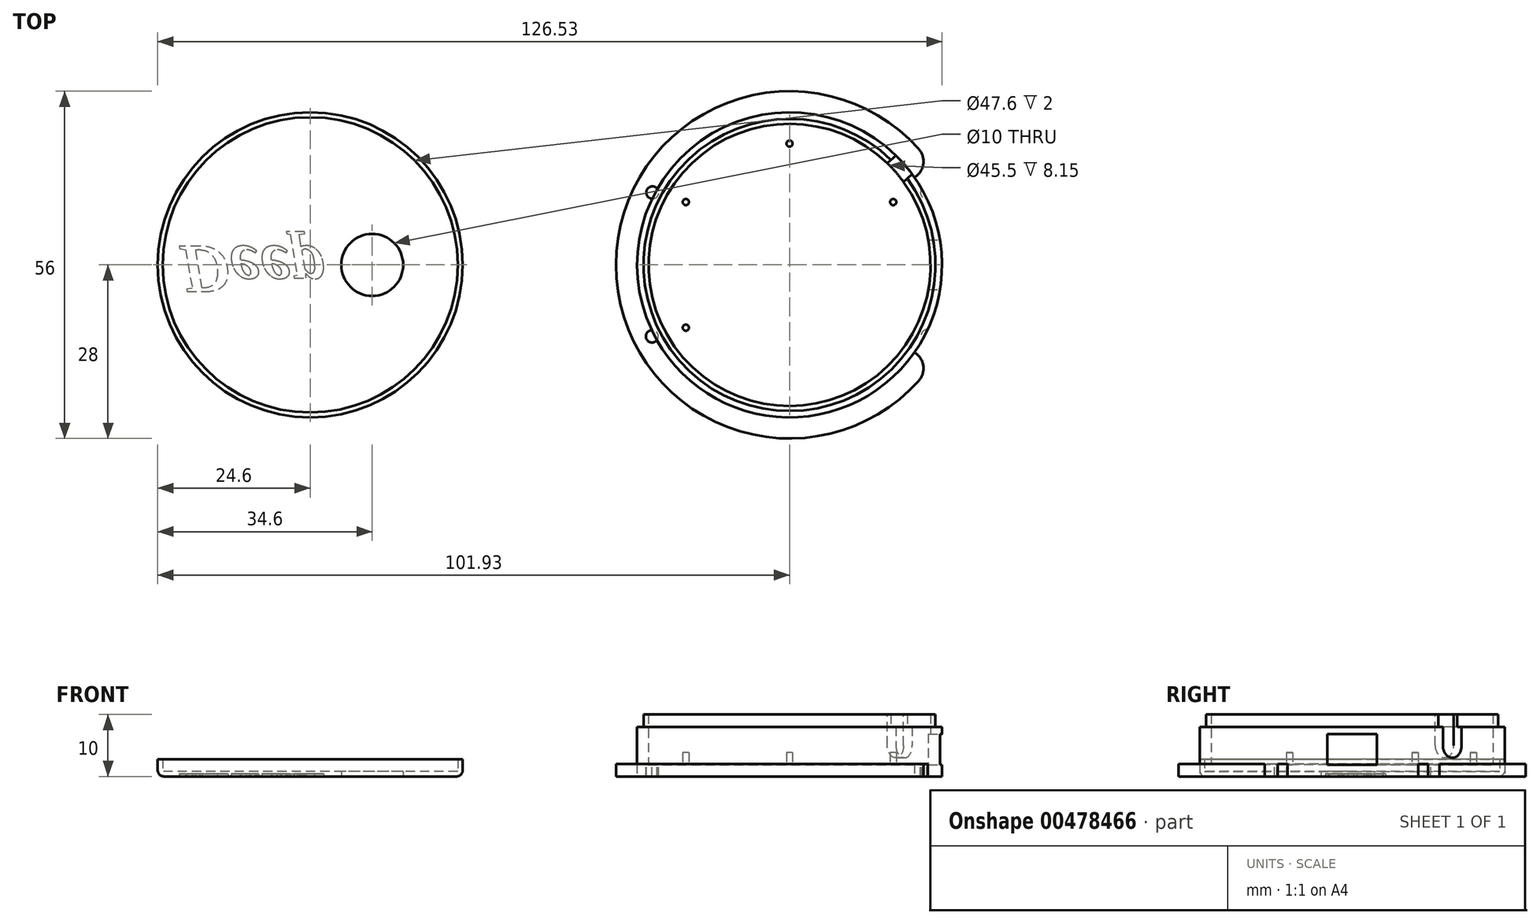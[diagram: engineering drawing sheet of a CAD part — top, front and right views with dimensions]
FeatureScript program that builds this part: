
annotation { "Feature Type Name" : "Feature", "Feature Type Description" : "" }
export const myFeature = defineFeature(function(context is Context, id is Id, definition is map)
    precondition{}
    {
        {
            var Q0;
            Q0=qCreatedBy(makeId("Top.planeOp"),FACE);
            var sketch = newSketch(context, id + "F0", { "sketchPlane" : qUnion([Q0])});
            skCircle(sketch, "E0", {"center": v(0, 0) * mm, "radius": 24.6 * mm});
            skSolve(sketch);
        }
        {
            var Q0;
            Q0=makeQuery(id+"F0.imprint","IMPRINT",FACE,{"disambiguationData":[TD([[makeQuery(id+"F0.imprint","IMPRINT",EDGE,{"derivedFrom":sQuery(id+"F0.wireOp",EDGE,"E0")}),1.0]])]});
            extrude(context, id + "F1", {"entities" : qUnion([Q0]), "depth" : 8 * mm});
        }
        {
            var Q0;
            Q0=makeQuery(id+"F1.opExtrude","CAP_FACE",FACE,{"disambiguationData":[OSD([sQuery(id+"F0.wireOp",EDGE,"E0")])],"isStart":false});
            shell(context, id + "F2", {"entities" : qUnion([Q0]), "thickness" : 1.85 * mm});
        }
        {
            var Q0;
            {var subQ0=sQuery(id+"F0.wireOp",EDGE,"E0");Q0=makeQuery(id+"F2.opShell","OFFSET_FACE",FACE,{"disambiguationData":[OSD([subQ0]),TDD([makeQuery(id+"F1.opExtrude","CAP_FACE",FACE,{"disambiguationData":[OSD([subQ0])],"isStart":true})])]});}
            var sketch = newSketch(context, id + "F3", { "sketchPlane" : qUnion([Q0])});
            skCircle(sketch, "E1", {"center": v(16.73, 10.13) * mm, "radius": 0.5 * mm});
            skCircle(sketch, "E2", {"center": v(0, 19.56) * mm, "radius": 0.5 * mm});
            skCircle(sketch, "E3", {"center": v(0, 0) * mm, "radius": 19.56 * mm, "construction": true});
            skCircle(sketch, "E4", {"center": v(-16.73, 10.13) * mm, "radius": 0.5 * mm});
            skCircle(sketch, "E5", {"center": v(-16.73, -10.13) * mm, "radius": 0.5 * mm});
            skLineSegment(sketch, "E6", {"start": v(-37.34, 0) * mm, "end": v(34.84, 0) * mm, "construction": true});
            skLineSegment(sketch, "E7", {"start": v(0, 0) * mm, "end": v(-16.73, 10.13) * mm, "construction": true});
            skLineSegment(sketch, "E8", {"start": v(0, 0) * mm, "end": v(-16.73, -10.13) * mm, "construction": true});
            skLineSegment(sketch, "E9", {"start": v(0, 0) * mm, "end": v(16.73, 10.13) * mm, "construction": true});
            skSolve(sketch);
        }
        {
            var Q0;
            Q0=makeQuery(id+"F3.imprint","IMPRINT",FACE,{"disambiguationData":[TD([[makeQuery(id+"F3.imprint","IMPRINT",EDGE,{"derivedFrom":sQuery(id+"F3.wireOp",EDGE,"E4")}),1.0]])]});
            var Q1;
            Q1=makeQuery(id+"F3.imprint","IMPRINT",FACE,{"disambiguationData":[TD([[makeQuery(id+"F3.imprint","IMPRINT",EDGE,{"derivedFrom":sQuery(id+"F3.wireOp",EDGE,"E5")}),1.0]])]});
            var Q2;
            Q2=makeQuery(id+"F3.imprint","IMPRINT",FACE,{"disambiguationData":[TD([[makeQuery(id+"F3.imprint","IMPRINT",EDGE,{"derivedFrom":sQuery(id+"F3.wireOp",EDGE,"E2")}),1.0]])]});
            var Q3;
            Q3=makeQuery(id+"F3.imprint","IMPRINT",FACE,{"disambiguationData":[TD([[makeQuery(id+"F3.imprint","IMPRINT",EDGE,{"derivedFrom":sQuery(id+"F3.wireOp",EDGE,"E1")}),1.0]])]});
            extrude(context, id + "F4", {"entities" : qUnion([Q0, Q1, Q2, Q3]), "operationType" : NewBodyOperationType.ADD, "depth" : 2 * mm});
        }
        {
            var Q0;
            {var subQ0=sQuery(id+"F0.wireOp",EDGE,"E0");Q0=makeQuery(id+"F2.opShell","OFFSET_FACE",FACE,{"disambiguationData":[OSD([subQ0]),TDD([makeQuery(id+"F1.opExtrude","CAP_FACE",FACE,{"disambiguationData":[OSD([subQ0])],"isStart":true})])]});}
            var sketch = newSketch(context, id + "F5", { "sketchPlane" : qUnion([Q0])});
            skLineSegment(sketch, "E10.bottom", {"start": v(19.14, 4) * mm, "end": v(26.14, 4) * mm});
            skLineSegment(sketch, "E10.top", {"start": v(19.14, -4) * mm, "end": v(26.14, -4) * mm});
            skLineSegment(sketch, "E10.left", {"start": v(19.14, 4) * mm, "end": v(19.14, -4) * mm});
            skLineSegment(sketch, "E10.right", {"start": v(26.14, 4) * mm, "end": v(26.14, -4) * mm});
            skSolve(sketch);
        }
        {
            var Q0;
            {var subQ0=sQuery(id+"F5.wireOp",EDGE,"E10.left");Q0=makeQuery(id+"F5.imprint","IMPRINT",FACE,{"disambiguationData":[TD([[makeQuery(id+"F5.imprint","IMPRINT",EDGE,{"derivedFrom":subQ0}),1.0]])]});}
            var Q1;
            {var subQ0=sQuery(id+"F5.wireOp",EDGE,"E10.right");Q1=makeQuery(id+"F5.imprint","IMPRINT",FACE,{"disambiguationData":[TD([[makeQuery(id+"F5.imprint","IMPRINT",EDGE,{"derivedFrom":subQ0}),-1.0]])]});}
            extrude(context, id + "F6", {"entities" : qUnion([Q0, Q1]), "operationType" : NewBodyOperationType.REMOVE, "depth" : 5 * mm});
        }
        {
            var Q0;
            Q0=makeQuery(id+"F1.opExtrude","CAP_FACE",FACE,{"disambiguationData":[OSD([sQuery(id+"F0.wireOp",EDGE,"E0")])],"isStart":false});
            var sketch = newSketch(context, id + "F7", { "sketchPlane" : qUnion([Q0])});
            skCircle(sketch, "E11", {"center": v(0, 0) * mm, "radius": 22.75 * mm});
            skCircle(sketch, "E12", {"center": v(0, 0) * mm, "radius": 23.55 * mm});
            skSolve(sketch);
        }
        {
            var Q0;
            Q0=makeQuery(id+"F7.imprint","IMPRINT",FACE,{"disambiguationData":[TD([[makeQuery(id+"F7.imprint","IMPRINT",EDGE,{"derivedFrom":sQuery(id+"F7.wireOp",EDGE,"E11")}),-1.0]])]});
            extrude(context, id + "F8", {"entities" : qUnion([Q0]), "operationType" : NewBodyOperationType.ADD, "depth" : 2 * mm});
        }
        {
            var Q0;
            Q0=makeQuery(id+"F1.opExtrude","CAP_FACE",FACE,{"disambiguationData":[OSD([sQuery(id+"F0.wireOp",EDGE,"E0")])],"isStart":true});
            var sketch = newSketch(context, id + "F9", { "sketchPlane" : qUnion([Q0])});
            skCircle(sketch, "E13", {"center": v(0, 0) * mm, "radius": 28 * mm});
            skLineSegment(sketch, "E14", {"start": v(0, 0) * mm, "end": v(22.94, 16.06) * mm});
            skLineSegment(sketch, "E15", {"start": v(22.94, 16.06) * mm, "end": v(0, 0) * mm});
            skLineSegment(sketch, "E16", {"start": v(0, 0) * mm, "end": v(26.31, 9.58) * mm});
            skLineSegment(sketch, "E17", {"start": v(0, 0) * mm, "end": v(0, 28) * mm, "construction": true});
            skLineSegment(sketch, "E18", {"start": v(0, 0) * mm, "end": v(-28, 0) * mm, "construction": true});
            skLineSegment(sketch, "E19", {"start": v(0, 0) * mm, "end": v(0, -28) * mm, "construction": true});
            skLineSegment(sketch, "E20", {"start": v(0, 0) * mm, "end": v(28, 0) * mm, "construction": true});
            skLineSegment(sketch, "E21", {"start": v(0, 0) * mm, "end": v(26.31, -9.58) * mm});
            skLineSegment(sketch, "E22", {"start": v(0, 0) * mm, "end": v(22.94, -16.06) * mm});
            skLineSegment(sketch, "E23", {"start": v(0, 0) * mm, "end": v(-22.94, 16.06) * mm});
            skLineSegment(sketch, "E24", {"start": v(0, 0) * mm, "end": v(-26.31, 9.58) * mm});
            skLineSegment(sketch, "E25", {"start": v(0, 0) * mm, "end": v(-26.31, -9.58) * mm});
            skLineSegment(sketch, "E26", {"start": v(0, 0) * mm, "end": v(-22.94, -16.06) * mm});
            skSolve(sketch);
        }
        {
            var Q0;
            {var subQ0=sQuery(id+"F9.wireOp",EDGE,"E23");var subQ1=sQuery(id+"F9.wireOp",EDGE,"E13");var subQ2=makeQuery(id+"F9.imprint","INTERSECT",VERTEX,{"derivedFrom":[subQ1,subQ0]});Q0=makeQuery(id+"F9.imprint","IMPRINT",FACE,{"disambiguationData":[TD([[makeQuery(id+"F9.imprint","IMPRINT",EDGE,{"disambiguationData":[TD([[subQ2,-1.0]])],"derivedFrom":subQ1}),1.0]])]});}
            var Q1;
            {var subQ0=sQuery(id+"F9.wireOp",EDGE,"E15");var subQ1=sQuery(id+"F9.wireOp",EDGE,"E13");var subQ2=makeQuery(id+"F9.imprint","INTERSECT",VERTEX,{"derivedFrom":[subQ1,subQ0]});Q1=makeQuery(id+"F9.imprint","IMPRINT",FACE,{"disambiguationData":[TD([[makeQuery(id+"F9.imprint","IMPRINT",EDGE,{"disambiguationData":[TD([[subQ2,1.0]])],"derivedFrom":subQ1}),1.0]])]});}
            var Q2;
            {var subQ0=sQuery(id+"F9.wireOp",EDGE,"E21");var subQ1=sQuery(id+"F9.wireOp",EDGE,"E13");var subQ2=makeQuery(id+"F9.imprint","INTERSECT",VERTEX,{"derivedFrom":[subQ1,subQ0]});Q2=makeQuery(id+"F9.imprint","IMPRINT",FACE,{"disambiguationData":[TD([[makeQuery(id+"F9.imprint","IMPRINT",EDGE,{"disambiguationData":[TD([[subQ2,1.0]])],"derivedFrom":subQ1}),1.0]])]});}
            var Q3;
            {var subQ0=sQuery(id+"F9.wireOp",EDGE,"E25");var subQ1=sQuery(id+"F9.wireOp",EDGE,"E13");var subQ2=makeQuery(id+"F9.imprint","INTERSECT",VERTEX,{"derivedFrom":[subQ1,subQ0]});Q3=makeQuery(id+"F9.imprint","IMPRINT",FACE,{"disambiguationData":[TD([[makeQuery(id+"F9.imprint","IMPRINT",EDGE,{"disambiguationData":[TD([[subQ2,-1.0]])],"derivedFrom":subQ1}),1.0]])]});}
            extrude(context, id + "F10", {"entities" : qUnion([Q0, Q1, Q2, Q3]), "oppositeDirection" : true, "depth" : 2 * mm});
        }
        {
            var Q0;
            Q0=makeQuery(id+"F10.opExtrude","CAP_FACE",FACE,{"disambiguationData":[OSD([sQuery(id+"F0.wireOp",EDGE,"E0"),sQuery(id+"F9.wireOp",EDGE,"E13"),sQuery(id+"F9.wireOp",EDGE,"E25"),sQuery(id+"F9.wireOp",EDGE,"E26")])],"isStart":false});
            var sketch = newSketch(context, id + "F11", { "sketchPlane" : qUnion([Q0])});
            skCircle(sketch, "E27", {"center": v(0, 0) * mm, "radius": 25 * mm, "construction": true});
            skCircle(sketch, "E28", {"center": v(-22.11, 11.66) * mm, "radius": 1 * mm});
            skCircle(sketch, "E29", {"center": v(-22.18, -11.53) * mm, "radius": 1 * mm});
            skCircle(sketch, "E30", {"center": v(22.24, -11.42) * mm, "radius": 1 * mm});
            skCircle(sketch, "E31", {"center": v(22.13, 11.64) * mm, "radius": 1 * mm});
            skSolve(sketch);
        }
        {
            var Q0;
            Q0=makeQuery(id+"F11.imprint","IMPRINT",FACE,{"disambiguationData":[TD([[makeQuery(id+"F11.imprint","IMPRINT",EDGE,{"derivedFrom":sQuery(id+"F11.wireOp",EDGE,"E28")}),1.0]])]});
            var Q1;
            Q1=makeQuery(id+"F11.imprint","IMPRINT",FACE,{"disambiguationData":[TD([[makeQuery(id+"F11.imprint","IMPRINT",EDGE,{"derivedFrom":sQuery(id+"F11.wireOp",EDGE,"E29")}),1.0]])]});
            var Q2;
            Q2=makeQuery(id+"F11.imprint","IMPRINT",FACE,{"disambiguationData":[TD([[makeQuery(id+"F11.imprint","IMPRINT",EDGE,{"derivedFrom":sQuery(id+"F11.wireOp",EDGE,"E31")}),1.0]])]});
            var Q3;
            Q3=makeQuery(id+"F11.imprint","IMPRINT",FACE,{"disambiguationData":[TD([[makeQuery(id+"F11.imprint","IMPRINT",EDGE,{"derivedFrom":sQuery(id+"F11.wireOp",EDGE,"E30")}),1.0]])]});
            extrude(context, id + "F12", {"entities" : qUnion([Q0, Q1, Q2, Q3]), "operationType" : NewBodyOperationType.REMOVE, "oppositeDirection" : true, "depth" : 2 * mm});
        }
        {
            var Q0;
            Q0=makeQuery(id+"F10.opExtrude","SWEPT_EDGE",EDGE,{"disambiguationData":[OSD([sQuery(id+"F9.wireOp",EDGE,"E13"),sQuery(id+"F9.wireOp",EDGE,"E23")])]});
            var Q1;
            Q1=makeQuery(id+"F10.opExtrude","SWEPT_EDGE",EDGE,{"disambiguationData":[OSD([sQuery(id+"F9.wireOp",EDGE,"E13"),sQuery(id+"F9.wireOp",EDGE,"E24")])]});
            var Q2;
            Q2=makeQuery(id+"F10.opExtrude","SWEPT_EDGE",EDGE,{"disambiguationData":[OSD([sQuery(id+"F9.wireOp",EDGE,"E13"),sQuery(id+"F9.wireOp",EDGE,"E25")])]});
            var Q3;
            Q3=makeQuery(id+"F10.opExtrude","SWEPT_EDGE",EDGE,{"disambiguationData":[OSD([sQuery(id+"F9.wireOp",EDGE,"E13"),sQuery(id+"F9.wireOp",EDGE,"E26")])]});
            var Q4;
            Q4=makeQuery(id+"F10.opExtrude","SWEPT_EDGE",EDGE,{"disambiguationData":[OSD([sQuery(id+"F9.wireOp",EDGE,"E13"),sQuery(id+"F9.wireOp",EDGE,"E22")])]});
            var Q5;
            Q5=makeQuery(id+"F10.opExtrude","SWEPT_EDGE",EDGE,{"disambiguationData":[OSD([sQuery(id+"F9.wireOp",EDGE,"E13"),sQuery(id+"F9.wireOp",EDGE,"E21")])]});
            var Q6;
            Q6=makeQuery(id+"F10.opExtrude","SWEPT_EDGE",EDGE,{"disambiguationData":[OSD([sQuery(id+"F9.wireOp",EDGE,"E13"),sQuery(id+"F9.wireOp",EDGE,"E16")])]});
            var Q7;
            Q7=makeQuery(id+"F10.opExtrude","SWEPT_EDGE",EDGE,{"disambiguationData":[OSD([sQuery(id+"F9.wireOp",EDGE,"E13"),sQuery(id+"F9.wireOp",EDGE,"E15")])]});
            fillet(context, id + "F13", {"entities" : qUnion([Q0, Q1, Q2, Q3, Q4, Q5, Q6, Q7]), "radius" : 3 * mm, "tangentPropagation" : true, "allowEdgeOverflow" : false});
        }
        {
            var Q0;
            Q0=makeQuery(id+"F8.opExtrude","CAP_FACE",FACE,{"disambiguationData":[OSD([sQuery(id+"F7.wireOp",EDGE,"E11"),sQuery(id+"F7.wireOp",EDGE,"E12")])],"isStart":false});
            var sketch = newSketch(context, id + "F14", { "sketchPlane" : qUnion([Q0])});
            skLineSegment(sketch, "E32", {"start": v(13, 13.86) * mm, "end": v(18.99, 19.32) * mm});
            skLineSegment(sketch, "E33", {"start": v(18.99, 19.32) * mm, "end": v(21.68, 16.36) * mm});
            skLineSegment(sketch, "E34", {"start": v(21.68, 16.36) * mm, "end": v(15.38, 10.61) * mm});
            skLineSegment(sketch, "E35", {"start": v(15.38, 10.61) * mm, "end": v(13, 13.86) * mm});
            skSolve(sketch);
        }
        {
            var Q0;
            {var subQ0=sQuery(id+"F14.wireOp",EDGE,"kEsMgIN9-urI5-DtvO-p9EU-ntrXV4kS493W");Q0=makeQuery(id+"F14.imprint","IMPRINT",FACE,{"disambiguationData":[TD([[makeQuery(id+"F14.imprint","IMPRINT",EDGE,{"derivedFrom":subQ0}),1.0]])]});}
            var Q1;
            {var subQ0=sQuery(id+"F14.wireOp",EDGE,"E32");var subQ1=makeQuery(id+"F8.opExtrude","CAP_EDGE",EDGE,{"disambiguationData":[OSD([sQuery(id+"F7.wireOp",EDGE,"E12")])],"isStart":false});var subQ2=makeQuery(id+"F14.imprint","INTERSECT",VERTEX,{"derivedFrom":[subQ1,subQ0]});Q1=makeQuery(id+"F14.imprint","IMPRINT",FACE,{"disambiguationData":[TD([[makeQuery(id+"F14.imprint","IMPRINT",EDGE,{"disambiguationData":[TD([[subQ2,1.0]])],"derivedFrom":subQ0}),-1.0]])]});}
            var Q2;
            {var subQ0=sQuery(id+"F14.wireOp",EDGE,"E33");Q2=makeQuery(id+"F14.imprint","IMPRINT",FACE,{"disambiguationData":[TD([[makeQuery(id+"F14.imprint","IMPRINT",EDGE,{"derivedFrom":subQ0}),-1.0]])]});}
            extrude(context, id + "F15", {"entities" : qUnion([Q0, Q1, Q2]), "operationType" : NewBodyOperationType.REMOVE, "oppositeDirection" : true, "depth" : 7 * mm});
        }
        {
            var Q0;
            Q0=makeQuery(id+"F15.boolean.opBoolean","COPY",EDGE,{"derivedFrom":makeQuery(id+"F15.opExtrude","CAP_EDGE",EDGE,{"disambiguationData":[OSD([sQuery(id+"F14.wireOp",EDGE,"E32")])],"isStart":false})});
            var Q1;
            Q1=makeQuery(id+"F15.boolean.opBoolean","COPY",EDGE,{"derivedFrom":makeQuery(id+"F15.opExtrude","CAP_EDGE",EDGE,{"disambiguationData":[OSD([sQuery(id+"F14.wireOp",EDGE,"E34")])],"isStart":false})});
            fillet(context, id + "F16", {"entities" : qUnion([Q0, Q1]), "radius" : 2 * mm, "tangentPropagation" : true, "allowEdgeOverflow" : false});
        }
        {
            var Q0;
            Q0=qCreatedBy(makeId("Top.planeOp"),FACE);
            var sketch = newSketch(context, id + "F17", { "sketchPlane" : qUnion([Q0])});
            skCircle(sketch, "E36", {"center": v(-77.33, 0) * mm, "radius": 24.6 * mm});
            skSolve(sketch);
        }
        {
            var Q0;
            Q0=makeQuery(id+"F17.imprint","IMPRINT",FACE,{"disambiguationData":[TD([[makeQuery(id+"F17.imprint","IMPRINT",EDGE,{"derivedFrom":sQuery(id+"F17.wireOp",EDGE,"E36")}),1.0]])]});
            extrude(context, id + "F18", {"entities" : qUnion([Q0]), "depth" : 2.8 * mm});
        }
        {
            var Q0;
            Q0=makeQuery(id+"F18.opExtrude","CAP_FACE",FACE,{"disambiguationData":[OSD([sQuery(id+"F17.wireOp",EDGE,"E36")])],"isStart":false});
            shell(context, id + "F19", {"entities" : qUnion([Q0]), "thickness" : .8 * mm});
        }
        {
            var Q0;
            Q0=makeQuery(id+"F18.opExtrude","CAP_FACE",FACE,{"disambiguationData":[OSD([sQuery(id+"F17.wireOp",EDGE,"E36")])],"isStart":true});
            var sketch = newSketch(context, id + "F20", { "sketchPlane" : qUnion([Q0])});
            skLineSegment(sketch, "E37", {"start": v(-77.33, 0) * mm, "end": v(-77.33, 55.52) * mm});
            skCircle(sketch, "E38", {"center": v(-67.33, 0) * mm, "radius": 5 * mm});
            skSolve(sketch);
        }
        {
            var Q0;
            Q0=makeQuery(id+"F20.imprint","IMPRINT",FACE,{"disambiguationData":[TD([[makeQuery(id+"F20.imprint","IMPRINT",EDGE,{"derivedFrom":sQuery(id+"F20.wireOp",EDGE,"E38")}),1.0]])]});
            extrude(context, id + "F21", {"entities" : qUnion([Q0]), "operationType" : NewBodyOperationType.REMOVE, "oppositeDirection" : true, "depth" : 1.5 * mm});
        }
        {
            var Q0;
            Q0=makeQuery(id+"F18.opExtrude","CAP_EDGE",EDGE,{"disambiguationData":[OSD([sQuery(id+"F17.wireOp",EDGE,"E36")])],"isStart":true});
            fillet(context, id + "F22", {"entities" : qUnion([Q0]), "radius" : 1 * mm, "tangentPropagation" : true, "allowEdgeOverflow" : false});
        }
        {
            var Q0;
            Q0=makeQuery(id+"F18.opExtrude","CAP_FACE",FACE,{"disambiguationData":[OSD([sQuery(id+"F17.wireOp",EDGE,"E36")])],"isStart":true});
            var sketch = newSketch(context, id + "F23", { "sketchPlane" : qUnion([Q0])});
            skText(sketch, "E39", { "text": "Deep", "fontName": "Tinos-BoldItalic.ttf"});
            const initialGuessF23  = {"E39": [-0.0984, -0.003, 1, 0, 0.00804]};
            skSetInitialGuess(sketch, initialGuessF23);
            skSolve(sketch);
        }
        {
            var Q0;
            Q0 = qSketchRegion(id + "F23", true);
            extrude(context, id + "F24", {"entities" : qUnion([Q0]), "operationType" : NewBodyOperationType.REMOVE, "oppositeDirection" : true, "depth" : 0.4 * mm});
        }
    });
